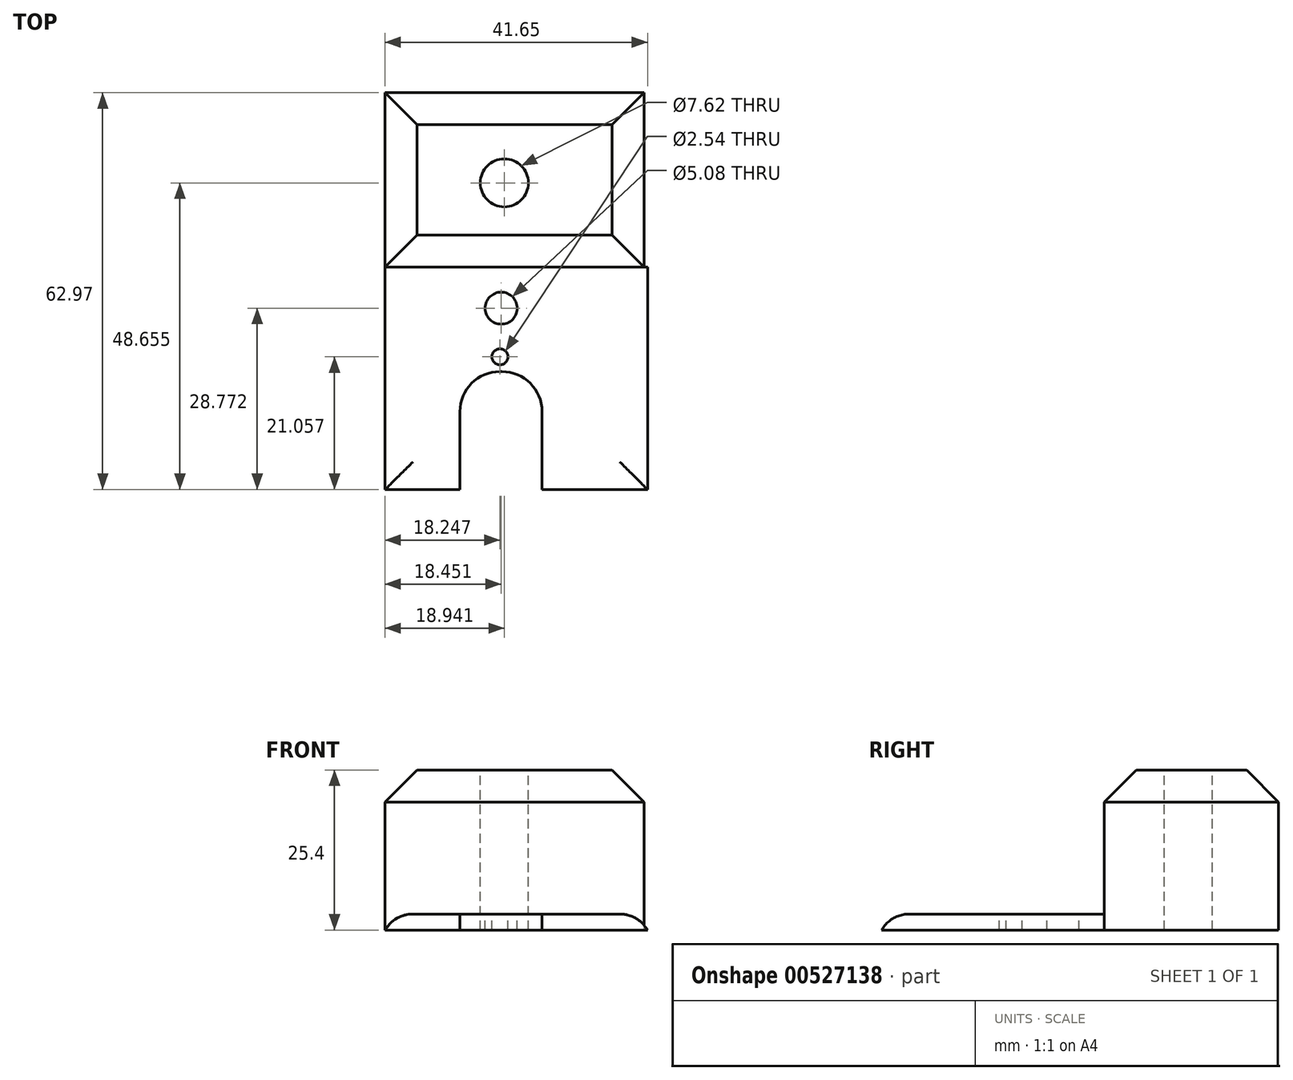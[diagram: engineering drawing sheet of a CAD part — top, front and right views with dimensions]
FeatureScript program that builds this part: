
annotation { "Feature Type Name" : "Feature", "Feature Type Description" : "" }
export const myFeature = defineFeature(function(context is Context, id is Id, definition is map)
    precondition{}
    {
        {
            var Q0;
            Q0=qCreatedBy(makeId("Top.planeOp"),FACE);
            var sketch = newSketch(context, id + "F0", { "sketchPlane" : qUnion([Q0])});
            skLineSegment(sketch, "E0.bottom", {"start": v(-24.92, 27.67) * mm, "end": v(16.18, 27.67) * mm});
            skLineSegment(sketch, "E0.top", {"start": v(-24.92, 0) * mm, "end": v(16.18, 0) * mm});
            skLineSegment(sketch, "E0.left", {"start": v(-24.92, 27.67) * mm, "end": v(-24.92, 0) * mm});
            skLineSegment(sketch, "E0.right", {"start": v(16.18, 27.67) * mm, "end": v(16.18, 0) * mm});
            skSolve(sketch);
        }
        {
            var Q0;
            Q0 = qSketchRegion(id + "F0", true);
            extrude(context, id + "F1", {"entities" : qUnion([Q0]), "depth" : 25.4 * mm, "offsetDistance" : 25.4 * mm});
        }
        {
            var Q0;
            Q0=qCreatedBy(makeId("Top.planeOp"),FACE);
            var sketch = newSketch(context, id + "F2", { "sketchPlane" : qUnion([Q0])});
            skLineSegment(sketch, "E1.bottom", {"start": v(-24.87, 0) * mm, "end": v(16.73, 0) * mm});
            skLineSegment(sketch, "E1.top", {"start": v(-24.87, -35.3) * mm, "end": v(16.73, -35.3) * mm});
            skLineSegment(sketch, "E1.left", {"start": v(-24.87, 0) * mm, "end": v(-24.87, -35.3) * mm});
            skLineSegment(sketch, "E1.right", {"start": v(16.73, 0) * mm, "end": v(16.73, -35.3) * mm});
            skSolve(sketch);
        }
        {
            var Q0;
            Q0 = qSketchRegion(id + "F2", true);
            extrude(context, id + "F3", {"entities" : qUnion([Q0]), "operationType" : NewBodyOperationType.ADD, "depth" : 2.54 * mm, "offsetDistance" : 25.4 * mm});
        }
        {
            var Q0;
            Q0=makeQuery(id+"F3.opExtrude","CAP_FACE",FACE,{"disambiguationData":[OSD([sQuery(id+"F2.wireOp",EDGE,"E1.bottom"),sQuery(id+"F2.wireOp",EDGE,"E1.top"),sQuery(id+"F2.wireOp",EDGE,"E1.left"),sQuery(id+"F2.wireOp",EDGE,"E1.right")])],"isStart":false});
            var sketch = newSketch(context, id + "F4", { "sketchPlane" : qUnion([Q0])});
            skLineSegment(sketch, "E2", {"start": v(-13.02, -45.53) * mm, "end": v(-13.02, -22.94) * mm});
            skLineSegment(sketch, "E3", {"start": v(-6.67, -16.6) * mm, "end": v(-6.34, -16.6) * mm});
            skLineSegment(sketch, "E4", {"start": v(0, -22.94) * mm, "end": v(0, -45.53) * mm});
            skLineSegment(sketch, "E5", {"start": v(0, -45.53) * mm, "end": v(-13.02, -45.53) * mm});
            skPoint(sketch, "E6.visualSharp", {"position": v(-13.02, -16.6) * mm});
            skArc(sketch, "E6.filletArc", {"start": v(-6.67, -16.6) * mm, "mid": v(-11.16, -18.45) * mm, "end": v(-13.02, -22.94) * mm});
            skPoint(sketch, "E7.visualSharp", {"position": v(0, -16.6) * mm});
            skArc(sketch, "E7.filletArc", {"start": v(0, -22.94) * mm, "mid": v(-1.85, -18.45) * mm, "end": v(-6.34, -16.6) * mm});
            skSolve(sketch);
        }
        {
            var Q0;
            Q0 = qSketchRegion(id + "F4", true);
            extrude(context, id + "F5", {"entities" : qUnion([Q0]), "operationType" : NewBodyOperationType.REMOVE, "oppositeDirection" : true, "depth" : 25.4 * mm, "offsetDistance" : 25.4 * mm});
        }
        {
            var Q0;
            Q0=makeQuery(id+"F1.opExtrude","CAP_FACE",FACE,{"disambiguationData":[OSD([sQuery(id+"F0.wireOp",EDGE,"E0.bottom"),sQuery(id+"F0.wireOp",EDGE,"E0.top"),sQuery(id+"F0.wireOp",EDGE,"E0.left"),sQuery(id+"F0.wireOp",EDGE,"E0.right")])],"isStart":false});
            var sketch = newSketch(context, id + "F6", { "sketchPlane" : qUnion([Q0])});
            skPoint(sketch, "E8", {"position": v(-5.98, 13.36) * mm});
            skPoint(sketch, "E9", {"position": v(0, -13.3) * mm});
            skPoint(sketch, "E10", {"position": v(0, -18.09) * mm});
            skSolve(sketch);
        }
        {
            var Q0;
            Q0=sQuery(id+"F6.wireOp",VERTEX,"E8");
            var Q1;
            Q1=makeQuery(id+"F1.opExtrude","SWEPT_BODY",BODY,{"disambiguationData":[OSD([sQuery(id+"F0.wireOp",EDGE,"E0.bottom"),sQuery(id+"F0.wireOp",EDGE,"E0.top"),sQuery(id+"F0.wireOp",EDGE,"E0.left"),sQuery(id+"F0.wireOp",EDGE,"E0.right")])]});
            hole(context, id + "F7", {"style" : HoleStyle.SIMPLE, "endStyle" : HoleEndStyle.BLIND, "holeDiameter" : 7.62 * mm, "holeDepth" : 508 * mm, "isTappedThrough" : true, "tappedDepth" : 12.7 * mm, "tapClearance" : 3, "locations" : qUnion([Q0]), "scope" : qUnion([Q1])});
        }
        {
            var Q0;
            Q0=makeQuery(id+"F3.opExtrude","CAP_FACE",FACE,{"disambiguationData":[OSD([sQuery(id+"F2.wireOp",EDGE,"E1.bottom"),sQuery(id+"F2.wireOp",EDGE,"E1.top"),sQuery(id+"F2.wireOp",EDGE,"E1.left"),sQuery(id+"F2.wireOp",EDGE,"E1.right")])],"isStart":false});
            var sketch = newSketch(context, id + "F8", { "sketchPlane" : qUnion([Q0])});
            skPoint(sketch, "E11", {"position": v(-6.67, -14.24) * mm});
            skPoint(sketch, "E12", {"position": v(-6.67, -8.13) * mm});
            skSolve(sketch);
        }
        {
            var Q0;
            Q0=sQuery(id+"F8.wireOp",VERTEX,"E11");
            var Q1;
            Q1=makeQuery(id+"F1.opExtrude","SWEPT_BODY",BODY,{"disambiguationData":[OSD([sQuery(id+"F0.wireOp",EDGE,"E0.bottom"),sQuery(id+"F0.wireOp",EDGE,"E0.top"),sQuery(id+"F0.wireOp",EDGE,"E0.left"),sQuery(id+"F0.wireOp",EDGE,"E0.right")])]});
            hole(context, id + "F9", {"style" : HoleStyle.SIMPLE, "endStyle" : HoleEndStyle.BLIND, "holeDiameter" : 2.54 * mm, "holeDepth" : 508 * mm, "isTappedThrough" : true, "tappedDepth" : 12.7 * mm, "tapClearance" : 3, "locations" : qUnion([Q0]), "scope" : qUnion([Q1])});
        }
        {
            var Q0;
            Q0=makeQuery(id+"F3.opExtrude","CAP_FACE",FACE,{"disambiguationData":[OSD([sQuery(id+"F2.wireOp",EDGE,"E1.bottom"),sQuery(id+"F2.wireOp",EDGE,"E1.top"),sQuery(id+"F2.wireOp",EDGE,"E1.left"),sQuery(id+"F2.wireOp",EDGE,"E1.right")])],"isStart":false});
            var sketch = newSketch(context, id + "F10", { "sketchPlane" : qUnion([Q0])});
            skPoint(sketch, "E13", {"position": v(-6.47, -6.53) * mm});
            skSolve(sketch);
        }
        {
            var Q0;
            Q0=sQuery(id+"F10.wireOp",VERTEX,"E13");
            var Q1;
            Q1=makeQuery(id+"F1.opExtrude","SWEPT_BODY",BODY,{"disambiguationData":[OSD([sQuery(id+"F0.wireOp",EDGE,"E0.bottom"),sQuery(id+"F0.wireOp",EDGE,"E0.top"),sQuery(id+"F0.wireOp",EDGE,"E0.left"),sQuery(id+"F0.wireOp",EDGE,"E0.right")])]});
            hole(context, id + "F11", {"style" : HoleStyle.SIMPLE, "endStyle" : HoleEndStyle.BLIND, "holeDiameter" : 5.08 * mm, "holeDepth" : 508 * mm, "isTappedThrough" : true, "tappedDepth" : 12.7 * mm, "tapClearance" : 3, "locations" : qUnion([Q0]), "scope" : qUnion([Q1])});
        }
        {
            var Q0;
            Q0=makeQuery(id+"F1.opExtrude","CAP_EDGE",EDGE,{"disambiguationData":[OSD([sQuery(id+"F0.wireOp",EDGE,"E0.top")])],"isStart":false});
            var Q1;
            Q1=makeQuery(id+"F1.opExtrude","CAP_EDGE",EDGE,{"disambiguationData":[OSD([sQuery(id+"F0.wireOp",EDGE,"E0.right")])],"isStart":false});
            var Q2;
            Q2=makeQuery(id+"F1.opExtrude","CAP_EDGE",EDGE,{"disambiguationData":[OSD([sQuery(id+"F0.wireOp",EDGE,"E0.bottom")])],"isStart":false});
            var Q3;
            Q3=makeQuery(id+"F1.opExtrude","CAP_EDGE",EDGE,{"disambiguationData":[OSD([sQuery(id+"F0.wireOp",EDGE,"E0.left")])],"isStart":false});
            chamfer(context, id + "F12", {"entities" : qUnion([Q0, Q1, Q2, Q3]), "width" : 5.08 * mm, "tangentPropagation" : true});
        }
        {
            var Q0;
            Q0=makeQuery(id+"F3.opExtrude","CAP_EDGE",EDGE,{"disambiguationData":[OSD([sQuery(id+"F2.wireOp",EDGE,"E1.right")])],"isStart":false});
            var Q1;
            {var subQ0=sQuery(id+"F2.wireOp",EDGE,"E1.right");var subQ1=sQuery(id+"F2.wireOp",EDGE,"E1.top");Q1=makeQuery(id+"F5.boolean.opBoolean","SPLIT",EDGE,{"disambiguationData":[TD([makeQuery(id+"F3.opExtrude","SWEPT_FACE",FACE,{"disambiguationData":[OSD([subQ0])]})])],"derivedFrom":makeQuery(id+"F3.opExtrude","CAP_EDGE",EDGE,{"disambiguationData":[OSD([subQ1])],"isStart":false})});}
            var Q2;
            {var subQ0=sQuery(id+"F2.wireOp",EDGE,"E1.left");var subQ1=sQuery(id+"F2.wireOp",EDGE,"E1.top");Q2=makeQuery(id+"F5.boolean.opBoolean","SPLIT",EDGE,{"disambiguationData":[TD([makeQuery(id+"F3.opExtrude","SWEPT_FACE",FACE,{"disambiguationData":[OSD([subQ0])]})])],"derivedFrom":makeQuery(id+"F3.opExtrude","CAP_EDGE",EDGE,{"disambiguationData":[OSD([subQ1])],"isStart":false})});}
            var Q3;
            Q3=makeQuery(id+"F5.boolean.opBoolean","COPY",EDGE,{"derivedFrom":makeQuery(id+"F5.opExtrude","CAP_EDGE",EDGE,{"disambiguationData":[OSD([sQuery(id+"F4.wireOp",EDGE,"E4")])],"isStart":true})});
            var Q4;
            Q4=makeQuery(id+"F3.opExtrude","CAP_EDGE",EDGE,{"disambiguationData":[OSD([sQuery(id+"F2.wireOp",EDGE,"E1.left")])],"isStart":false});
            fillet(context, id + "F13", {"entities" : qUnion([Q0, Q1, Q2, Q3, Q4]), "radius" : 5.08 * mm, "tangentPropagation" : true, "allowEdgeOverflow" : false});
        }
    });
